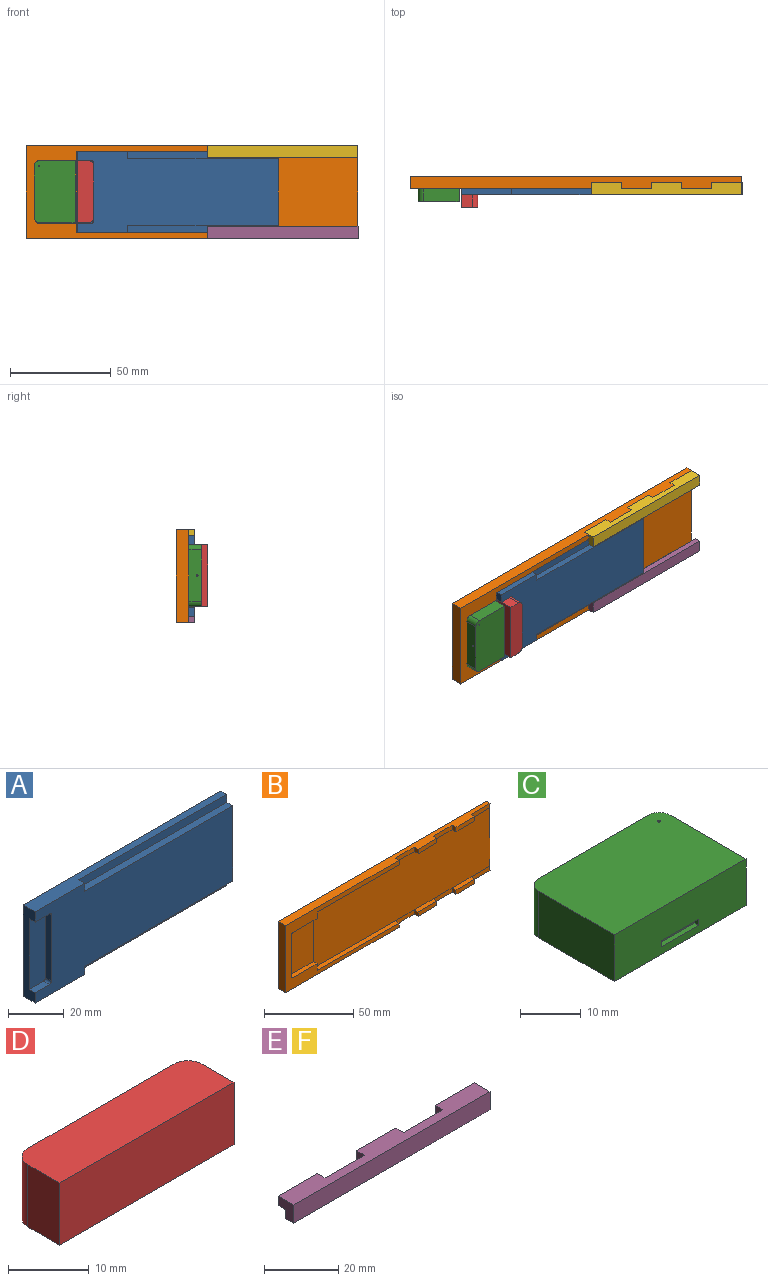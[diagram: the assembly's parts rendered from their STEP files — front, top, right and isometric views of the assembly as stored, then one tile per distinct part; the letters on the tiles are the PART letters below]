
ASSEMBLY  parts=6 mates=13
PART A: 18 faces, bbox 100x6x40 mm
  f0: plane 100x40mm, normal (0,-1,0), area 3221.2mm2, adj f1,f2,f3,f4,f6,f7,f8,f9
  f1: plane 100x5.99mm, normal (0,0,-1), area 374.6mm2, adj f0,f2,f3,f5,f15,f17
  f2: plane 40x5.99mm, normal (1,0,0), area 218.8mm2, adj f0,f1,f4,f5,f12,f13,f15,f16
  f3: plane 40x5.99mm, normal (-1,0,0), area 146.8mm2, adj f0,f1,f4,f5,f6,f7,f11
  f4: plane 100x5.99mm, normal (0,0,1), area 374.6mm2, adj f0,f2,f3,f5,f13,f14
  f5: plane 100x40mm, normal (0,1,0), area 4000mm2, adj f1,f2,f3,f4
  f6: plane 7.2x3mm, normal (0,0,-1), area 21.6mm2, adj f0,f3,f10,f11
  f7: plane 7.2x3mm, normal (0,0,1), area 21.6mm2, adj f0,f3,f8,f11
  f8: cylinder r=1mm len=3mm, axis (0,-1,0), area 4.7mm2, adj f0,f7,f9,f11
  f9: plane 29x3mm, normal (-1,0,0), area 87mm2, adj f0,f8,f10,f11
  f10: cylinder r=1mm len=3mm, axis (0,-1,0), area 4.7mm2, adj f0,f6,f9,f11
  f11: plane 31x8.2mm, normal (0,-1,0), area 253.8mm2, adj f3,f6,f7,f8,f9,f10
  f12: plane 75x3mm, normal (0,0,1), area 224.8mm2, adj f0,f2,f13,f14
  f13: plane 75x3.5mm, normal (0,-1,0), area 262.5mm2, adj f2,f4,f12,f14
  f14: plane 3.5x3mm, normal (1,0,0), area 10.5mm2, adj f0,f4,f12,f13
  f15: plane 75x3.5mm, normal (0,-1,0), area 262.5mm2, adj f1,f2,f16,f17
  f16: plane 75x3mm, normal (0,0,-1), area 224.8mm2, adj f0,f2,f15,f17
  f17: plane 3.5x3mm, normal (1,0,0), area 10.5mm2, adj f0,f1,f15,f16
PART B: 41 faces, bbox 165x6x46 mm
  f0: plane 15x3mm, normal (0,-1,0), area 45mm2, adj f11,f15,f31,f35
  f1: plane 15x3mm, normal (0,-1,0), area 45mm2, adj f5,f8,f29,f39
  f2: plane 15x3mm, normal (0,-1,0), area 45mm2, adj f5,f6,f26,f28
  f3: plane 15x3mm, normal (0,-1,0), area 45mm2, adj f10,f15,f32,f37
  f4: plane 46x3mm, normal (1,0,0), area 137.9mm2, adj f5,f15,f16,f18,f38,f40
  f5: plane 165x5.99mm, normal (0,0,1), area 854.2mm2, adj f1,f2,f4,f13,f14,f16,f25,f26
  f6: plane 15x3mm, normal (0,0,-1), area 45mm2, adj f2,f18,f26,f28
  f7: plane 65x3mm, normal (0,0,-1), area 194.8mm2, adj f12,f13,f18,f25
  f8: plane 15x3mm, normal (0,0,-1), area 45mm2, adj f1,f18,f29,f39
  f9: plane 65x3mm, normal (0,0,1), area 194.8mm2, adj f13,f17,f18,f34
  f10: plane 15x3mm, normal (0,0,1), area 45mm2, adj f3,f18,f32,f37
  f11: plane 15x3mm, normal (0,0,1), area 45mm2, adj f0,f18,f31,f35
  f12: plane 4.5x3mm, normal (1,0,0), area 13.5mm2, adj f7,f13,f18,f19
  f13: plane 90x46mm, normal (0,-1,0), area 920.4mm2, adj f5,f7,f9,f12,f14,f15,f17,f19
  f14: plane 46x5.99mm, normal (-1,0,0), area 275.7mm2, adj f5,f13,f15,f16
  f15: plane 165x5.99mm, normal (0,0,-1), area 854.2mm2, adj f0,f3,f4,f13,f14,f16,f31,f32
  f16: plane 165x46mm, normal (0,1,0), area 7590mm2, adj f4,f5,f14,f15
  f17: plane 4.5x3mm, normal (1,0,0), area 13.5mm2, adj f9,f13,f18,f23
  f18: plane 140x40mm, normal (0,-1,0), area 5600mm2, adj f4,f6,f7,f8,f9,f10,f11,f12
  f19: plane 19x3mm, normal (0,0,-1), area 56.9mm2, adj f12,f13,f20,f24
  f20: cylinder r=1mm len=3mm, axis (0,-1,0), area 4.7mm2, adj f13,f19,f21,f24
  f21: plane 29x3mm, normal (1,0,0), area 86.9mm2, adj f13,f20,f22,f24
  f22: cylinder r=1mm len=3mm, axis (0,-1,0), area 4.7mm2, adj f13,f21,f23,f24
  f23: plane 19x3mm, normal (0,0,1), area 56.9mm2, adj f13,f17,f22,f24
  f24: plane 31x20mm, normal (0,-1,0), area 619.6mm2, adj f18,f19,f20,f21,f22,f23
  f25: plane 3x3mm, normal (1,0,0), area 9mm2, adj f5,f7,f13,f27
  f26: plane 3x3mm, normal (-1,0,0), area 9mm2, adj f2,f5,f6,f27
  f27: plane 15x3mm, normal (0,-1,0), area 45mm2, adj f5,f18,f25,f26
  f28: plane 3x3mm, normal (1,0,0), area 9mm2, adj f2,f5,f6,f30
  f29: plane 3x3mm, normal (-1,0,0), area 9mm2, adj f1,f5,f8,f30
  f30: plane 15x3mm, normal (0,-1,0), area 45mm2, adj f5,f18,f28,f29
  f31: plane 3x3mm, normal (1,0,0), area 9mm2, adj f0,f11,f15,f33
  f32: plane 3x3mm, normal (-1,0,0), area 9mm2, adj f3,f10,f15,f33
  f33: plane 15x3mm, normal (0,-1,0), area 45mm2, adj f15,f18,f31,f32
  f34: plane 3x3mm, normal (1,0,0), area 9mm2, adj f9,f13,f15,f36
  f35: plane 3x3mm, normal (-1,0,0), area 9mm2, adj f0,f11,f15,f36
  f36: plane 15x3mm, normal (0,-1,0), area 45mm2, adj f15,f18,f34,f35
  f37: plane 3x3mm, normal (1,0,0), area 9mm2, adj f3,f10,f15,f38
  f38: plane 15x3mm, normal (0,-1,0), area 45mm2, adj f4,f15,f18,f37
  f39: plane 3x3mm, normal (1,0,0), area 9mm2, adj f1,f5,f8,f40
  f40: plane 15x3mm, normal (0,-1,0), area 45mm2, adj f4,f5,f18,f39
PART C: 17 faces, bbox 30.8x20.3x9.4 mm
  f0: plane 30.75x9.44mm, normal (0,-1,0), area 279.4mm2, adj f2,f3,f6,f7,f10,f11,f12,f13
  f1: cylinder r=2.5mm len=9.44mm, axis (0,0,-1), area 37.1mm2, adj f2,f5,f6,f7
  f2: plane 17.75x9.44mm, normal (-1,0,0), area 167.6mm2, adj f0,f1,f6,f7
  f3: plane 17.75x9.44mm, normal (1,0,0), area 167.6mm2, adj f0,f4,f6,f7
  f4: cylinder r=2.5mm len=9.44mm, axis (0,0,-1), area 37.1mm2, adj f3,f5,f6,f7
  f5: plane 25.75x9.44mm, normal (0,1,0), area 242.5mm2, adj f1,f4,f6,f7,f15
  f6: plane 30.75x20.25mm, normal (0,0,1), area 619.8mm2, adj f0,f1,f2,f3,f4,f5,f8
  f7: plane 30.75x20.25mm, normal (0,0,-1), area 620mm2, adj f0,f1,f2,f3,f4,f5
  f8: cylinder r=0.25mm len=5mm, axis (0,0,1), area 7.9mm2, adj f6,f9
  f9: plane 0.5x0.5mm, normal (0,0,1), area 0.2mm2, adj f8
  f10: plane 8.67x1mm, normal (0,0,-1), area 8.7mm2, adj f0,f11,f13,f14
  f11: plane 1.25x1mm, normal (1,0,0), area 1.2mm2, adj f0,f10,f12,f14
  f12: plane 8.67x1mm, normal (0,0,1), area 8.7mm2, adj f0,f11,f13,f14
  f13: plane 1.25x1mm, normal (-1,0,0), area 1.2mm2, adj f0,f10,f12,f14
  f14: plane 8.67x1.25mm, normal (0,-1,0), area 10.8mm2, adj f10,f11,f12,f13
  f15: cylinder r=0.43mm len=5mm, axis (0,1,0), area 13.6mm2, adj f5,f16
  f16: plane 0.86x0.86mm, normal (0,1,0), area 0.6mm2, adj f15
PART D: 8 faces, bbox 30.6x8.1x9.4 mm
  f0: cylinder r=2.5mm len=9.44mm, axis (0,0,-1), area 37.1mm2, adj f1,f5,f6,f7
  f1: plane 9.44x5.58mm, normal (-1,0,0), area 52.7mm2, adj f0,f2,f6,f7
  f2: plane 30.61x9.44mm, normal (0,-1,0), area 289mm2, adj f1,f3,f6,f7
  f3: plane 9.44x5.58mm, normal (1,0,0), area 52.7mm2, adj f2,f4,f6,f7
  f4: cylinder r=2.5mm len=9.44mm, axis (0,0,-1), area 37.1mm2, adj f3,f5,f6,f7
  f5: plane 25.61x9.44mm, normal (0,1,0), area 241.8mm2, adj f0,f4,f6,f7
  f6: plane 30.61x8.08mm, normal (0,0,1), area 244.6mm2, adj f0,f1,f2,f3,f4,f5
  f7: plane 30.61x8.08mm, normal (0,0,-1), area 244.6mm2, adj f0,f1,f2,f3,f4,f5
PART E: 16 faces, bbox 75x6x6 mm
  f0: plane 15x3mm, normal (0,0,-1), area 45mm2, adj f6,f9,f12,f14
  f1: plane 15x3mm, normal (0,0,-1), area 45mm2, adj f3,f10,f13,f14
  f2: plane 15x3mm, normal (0,0,-1), area 45mm2, adj f4,f7,f11,f14
  f3: plane 15x3mm, normal (0,1,0), area 45mm2, adj f1,f5,f10,f13
  f4: plane 15x3mm, normal (0,1,0), area 45mm2, adj f2,f5,f7,f11
  f5: plane 75x5.99mm, normal (0,0,1), area 359.6mm2, adj f3,f4,f6,f7,f8,f9,f10,f11
  f6: plane 6x5.99mm, normal (-1,0,0), area 27mm2, adj f0,f5,f8,f9,f14,f15
  f7: plane 6x5.99mm, normal (1,0,0), area 27mm2, adj f2,f4,f5,f8,f14,f15
  f8: plane 75x6mm, normal (0,-1,0), area 450mm2, adj f5,f6,f7,f15
  f9: plane 15x3mm, normal (0,1,0), area 45mm2, adj f0,f5,f6,f12
  f10: plane 3x3mm, normal (1,0,0), area 9mm2, adj f1,f3,f5,f14
  f11: plane 3x3mm, normal (-1,0,0), area 9mm2, adj f2,f4,f5,f14
  f12: plane 3x3mm, normal (1,0,0), area 9mm2, adj f0,f5,f9,f14
  f13: plane 3x3mm, normal (-1,0,0), area 9mm2, adj f1,f3,f5,f14
  f14: plane 75x6mm, normal (0,1,0), area 315mm2, adj f0,f1,f2,f5,f6,f7,f10,f11
  f15: plane 75x3mm, normal (0,0,-1), area 224.8mm2, adj f6,f7,f8,f14
PART F: same geometry as E
PLACE A t=(25.49,43.3,52.84)mm
PLACE B t=(0,52.29,49.84)mm
PLACE C rot(axis=(0.58,-0.58,0.58),120deg) t=(24.38,49.3,72.97)mm
PLACE D rot(axis=(0.58,0.58,-0.58),120deg) t=(25.61,46.3,73.04)mm
PLACE E rot(axis=(0,-1,0),180deg) t=(165,49.3,52.84)mm
PLACE F t=(90,49.3,92.84)mm
MATE planar F.f10 <-> B.f29  axis (1,0,0) through (135,47.8,94.34)mm
MATE planar E.f5 <-> B.f15  axis (0,0,-1) through (97.5,49.3,49.84)mm
MATE planar C.f7 <-> B.f24  axis (0,1,0) through (14.29,49.3,72.97)mm
MATE planar A.f5 <-> B.f18  axis (0,1,0) through (125.49,49.3,92.84)mm
MATE planar A.f11 <-> D.f7  axis (0,-1,0) through (29.58,46.3,72.84)mm
MATE planar D.f5 <-> A.f9  axis (1,0,0) through (33.69,41.58,73.04)mm
MATE planar A.f4 <-> B.f8  axis (0,0,1) through (67.99,47.2,92.84)mm
MATE planar F.f9 <-> B.f27  axis (0,1,0) through (97.5,49.3,94.34)mm
MATE planar E.f3 <-> B.f33  axis (0,1,0) through (127.5,49.3,49.84)mm
MATE planar E.f7 <-> B.f34  axis (-1,0,0) through (90,45.8,52.34)mm
MATE planar D.f1 <-> A.f6  axis (0,0,1) through (28.4,41.58,88.34)mm
MATE planar C.f3 <-> B.f19  axis (0,0,1) through (15.5,44.58,88.34)mm
MATE planar F.f5 <-> B.f5  axis (0,0,1) through (127.5,45.92,95.84)mm
